# Revit family: 2070024
name_source: partatom
category: Lighting Fixtures
revit_build: Autodesk Revit 2018 (Build: 20170223_1515(x64)
units: mm (PartAtom-declared; Revit-internal decimal feet)

## family parameters
Cut with Voids When Loaded = No
Host = Face
Light Source = No
OmniClass Number = 23.80.70.11.17
OmniClass Title = Specialized Lighting by Location or Use
Part Type = Normal
Room Calculation Point = No
Round Connector Dimension = Use Diameter
Shared = No

## types (12) — shared parameters
Apparent Load = 21 VA
Assembly Code = D5020200
Average Life = 50 000h
Body Material = Aluminum_Sylvania_Expospot_White
Body Secondary Material = Plastic_Sylvania_Expospot_Black
Colour Variation Initial = 3SDCM
Control Gear Mounting = Remote
Control Gear Required = No
Control Gear Type = Electronic
Cutout Diameter = 126 mm  [stored 0.413386 ft]
Description = Specifically designed for Retail and Display applications. I.e. Supermarkets Fashion Retail Department stores. Build around a 70mm reflector and lens combination.
Diameter = 137 mm  [stored 0.449475 ft]
Dimmable = N
Drive Current = 500mA
Electrical Protection = Class II
Glow Wire Test = 850 °C
Head Diameter = 85 mm  [stored 0.278871 ft]
Head Radius = 42.5 mm  [stored 0.139436 ft]
Height = 103 mm  [stored 0.337927 ft]
IK Rating = IK02
IP Rating = IP20
Inrush Current = 28 A
Inrush Duration = 139µs
LOR = 100%
Lamp = LED
Lamp Power Factor = 0.9
Light Loss Factor = 1
Manufacturer = Feilo Sylvania
Max. Luminaires per 10A B Breaker = 19
Max. Luminaires per 10A C Breaker = 31
Max. Luminaires per 13A B Breaker = 25
Max. Luminaires per 13A C Breaker = 41
Max. Luminaires per 16A B Breaker = 31
Max. Luminaires per 16A C Breaker = 51
Max. Luminaires per 20A B Breaker = 42
Max. Luminaires per 20A C Breaker = 70
Mounting Outer Radius = 45.5 mm  [stored 0.149278 ft]
Nominal Frequency = 50/60Hz
Photobiological Risk Group = RG1
Product Family = EXPOSPOT 70 ADJUSTABLE
Product Page URL = http://www.sylvania-lighting.com
Radius = 68.5 mm  [stored 0.224738 ft]
Reflector Material = Aluminum_Sylvania_Expospot_Polished
Total Power Consumption = 21 W
Voltage = 240 V
Voltage Comments = 220-240V~
Weight = 1 kg
zero-valued in all types: Default Elevation

## per-type parameters (varying)
| type | Beam Angle | CRI | Diffuser Material | Initial Color | Initial Intensity | Model | Photometric Web File | Product Code | URL |
| EXPOSPOT 70 ADJ 90 4K WB WHT | 52° | 90Ra | Acrylic_Sylvania_Expospot_4000K | 4000 K | 1988 lm | EXPOSPOT 70 ADJ 90 4K WB WHT | IES_Expospot_70_Adjustable : 0060248 | 0060248 | http://www.sylvania-lighting.com |
| EXPOSPOT 70 ADJ 90 4K MB WHT | 42° | 90Ra | Acrylic_Sylvania_Expospot_4000K | 4000 K | 1964 lm | EXPOSPOT 70 ADJ 90 4K MB WHT | IES_Expospot_70_Adjustable : 0060247 | 0060247 | http://www.sylvania-lighting.com |
| EXPOSPOT 70 ADJ 90 4K NB WHT | 24° | 90Ra | Acrylic_Sylvania_Expospot_4000K | 4000 K | 1751 lm | EXPOSPOT 70 ADJ 90 4K NB WHT | IES_Expospot_70_Adjustable : 0060246 | 0060246 | http://www.sylvania-lighting.com |
| EXPOSPOT 70 ADJ 90 3K WB WHT | 53° | 90Ra | Acrylic_Sylvania_Expospot_3000K | 3000 K | 1815 lm | EXPOSPOT 70 ADJ 90 3K WB WHT | IES_Expospot_70_Adjustable : 0060245 | 0060245 | http://www.sylvania-lighting.com |
| EXPOSPOT 70 ADJ 90 3K MB WHT | 42° | 90Ra | Acrylic_Sylvania_Expospot_3000K | 3000 K | 1793 lm | EXPOSPOT 70 ADJ 90 3K MB WHT | IES_Expospot_70_Adjustable : 0060244 | 0060244 | http://www.sylvania-lighting.com |
| EXPOSPOT 70 ADJ 90 3K NB WHT | 25° | 90Ra | Acrylic_Sylvania_Expospot_3000K | 3000 K | 1769 lm | EXPOSPOT 70 ADJ 90 3K NB WHT | IES_Expospot_70_Adjustable : 0060243 | 0060243 | http://www.sylvania-lighting.com |
| EXPOSPOT 70 ADJ 80 4K WB WHT | 54° | 80Ra | Acrylic_Sylvania_Expospot_4000K | 4000 K | 1987 lm | EXPOSPOT 70 ADJ 80 4K WB WHT | IES_Expospot_70_Adjustable : 0060242 | 0060242 | http://www.sylvania-lighting.com |
| EXPOSPOT 70 ADJ 80 4K MB WHT | 42° | 80Ra | Acrylic_Sylvania_Expospot_4000K | 4000 K | 2224 lm | EXPOSPOT 70 ADJ 80 4K MB WHT | IES_Expospot_70_Adjustable : 0060241 | 0060241 | http://www.sylvania-lighting.com |
| EXPOSPOT 70 ADJ 80 4K NB WHT | 25° | 80Ra | Acrylic_Sylvania_Expospot_4000K | 4000 K | 2201 lm | EXPOSPOT 70 ADJ 80 4K NB WHT | IES_Expospot_70_Adjustable : 0060240 | 0060240 | http://www.sylvania-lighting.com |
| EXPOSPOT 70 ADJ 80 3K WB WHT | 54° | 80Ra | Acrylic_Sylvania_Expospot_3000K | 3000 K | 2082 lm | EXPOSPOT 70 ADJ 80 3K WB WHT | IES_Expospot_70_Adjustable : 0060239 | 0060239 | http://www.sylvania-lighting.com |
| EXPOSPOT 70 ADJ 80 3K NB WHT | 43° | 80Ra | Acrylic_Sylvania_Expospot_3000K | 3000 K | 2149 lm | EXPOSPOT 70 ADJ 80 3K NB WHT | IES_Expospot_70_Adjustable : 0060237 | 0060237 | http://www.sylvania-lighting.com |
| 2070024 EXPOSPOT 70 ADJ RA90 4000K NB WHITE | 43° | 80Ra | Acrylic_Sylvania_Expospot_3000K | 3000 K | 2152 lm | EXPOSPOT 70 ADJUSTABLE RA90 4000K NB WHITE | IES_Expospot_70_Adjustable : 0060246 | 0060238 | 0.9 |

note: [stored X ft] marks values corroborated as IEEE doubles in the binary element streams (Revit-internal decimal feet)

## geometry (parser evidence)
native form markers: Sweep x6
no freeform markers — native parametric forms only
